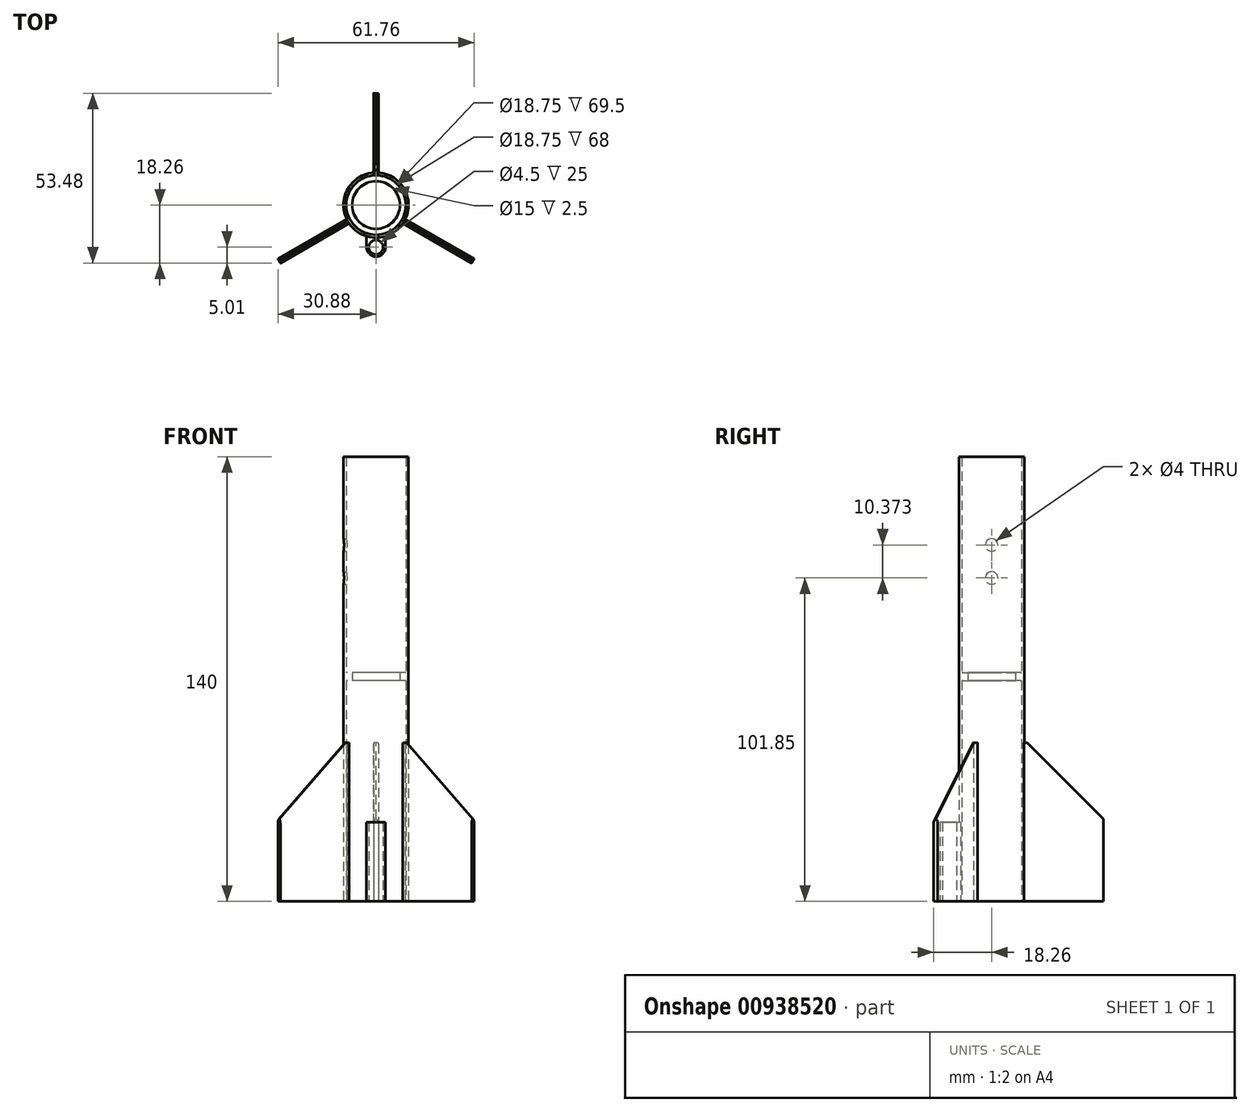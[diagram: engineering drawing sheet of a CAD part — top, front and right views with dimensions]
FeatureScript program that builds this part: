
annotation { "Feature Type Name" : "Feature", "Feature Type Description" : "" }
export const myFeature = defineFeature(function(context is Context, id is Id, definition is map)
    precondition{}
    {
        {
            var Q0;
            Q0=qCreatedBy(makeId("Top.planeOp"),FACE);
            var sketch = newSketch(context, id + "F0", { "sketchPlane" : qUnion([Q0])});
            skCircle(sketch, "E0", {"center": v(0, 0) * mm, "radius": 9.38 * mm});
            skCircle(sketch, "E1", {"center": v(0, 0) * mm, "radius": 10.25 * mm});
            skCircle(sketch, "E2", {"center": v(0, -13.25) * mm, "radius": 2.25 * mm});
            skCircle(sketch, "E3", {"center": v(0, -13.25) * mm, "radius": 3 * mm});
            skLineSegment(sketch, "E4", {"start": v(-3, -13.25) * mm, "end": v(-3, -9.8) * mm});
            skLineSegment(sketch, "E5", {"start": v(3, -13.25) * mm, "end": v(3, -9.8) * mm});
            skLineSegment(sketch, "E6.bottom", {"start": v(-0.75, 10.22) * mm, "end": v(0.75, 10.22) * mm, "construction": true});
            skLineSegment(sketch, "E6.top", {"start": v(-0.75, 35.22) * mm, "end": v(0.75, 35.22) * mm});
            skLineSegment(sketch, "E6.left", {"start": v(-0.75, 10.22) * mm, "end": v(-0.75, 35.22) * mm});
            skLineSegment(sketch, "E6.right", {"start": v(0.75, 10.22) * mm, "end": v(0.75, 35.22) * mm});
            skCircle(sketch, "E7", {"center": v(0, 0) * mm, "radius": 7.5 * mm});
            skSolve(sketch);
        }
        {
            var Q0;
            Q0=makeQuery(id+"F0.imprint","IMPRINT",FACE,{"disambiguationData":[TD([[makeQuery(id+"F0.imprint","IMPRINT",EDGE,{"derivedFrom":sQuery(id+"F0.wireOp",EDGE,"E0")}),-1.0]])]});
            extrude(context, id + "F1", {"entities" : qUnion([Q0]), "depth" : 140 * mm, "offsetDistance" : 25 * mm});
        }
        {
            var Q0;
            Q0=makeQuery(id+"F0.imprint","IMPRINT",FACE,{"disambiguationData":[TD([[makeQuery(id+"F0.imprint","IMPRINT",EDGE,{"derivedFrom":sQuery(id+"F0.wireOp",EDGE,"E6.top")}),-1.0]])]});
            extrude(context, id + "F2", {"entities" : qUnion([Q0]), "operationType" : NewBodyOperationType.ADD, "depth" : 50 * mm, "offsetDistance" : 25 * mm});
        }
        {
            var Q0;
            Q0=makeQuery(id+"F2.opExtrude","CAP_EDGE",EDGE,{"disambiguationData":[OSD([sQuery(id+"F0.wireOp",EDGE,"E6.top")])],"isStart":false});
            chamfer(context, id + "F3", {"entities" : qUnion([Q0]), "width" : 24 * mm, "tangentPropagation" : true});
        }
        {
            var Q0;
            Q0=makeQuery(id+"F3.opChamfer","BLEND_EDGE",EDGE,{"blendedFrom":[makeQuery(id+"F2.opExtrude","CAP_EDGE",EDGE,{"disambiguationData":[OSD([sQuery(id+"F0.wireOp",EDGE,"E6.top")])],"isStart":false}),makeQuery(id+"F2.opExtrude","SWEPT_FACE",FACE,{"disambiguationData":[OSD([sQuery(id+"F0.wireOp",EDGE,"E6.right")])]})],"blendedInto":[makeQuery(id+"F2.opExtrude","SWEPT_FACE",FACE,{"disambiguationData":[OSD([sQuery(id+"F0.wireOp",EDGE,"E6.right")])]})]});
            var Q1;
            Q1=makeQuery(id+"F3.opChamfer","BLEND_EDGE",EDGE,{"blendedFrom":[makeQuery(id+"F2.opExtrude","CAP_EDGE",EDGE,{"disambiguationData":[OSD([sQuery(id+"F0.wireOp",EDGE,"E6.top")])],"isStart":false}),makeQuery(id+"F2.opExtrude","SWEPT_FACE",FACE,{"disambiguationData":[OSD([sQuery(id+"F0.wireOp",EDGE,"E6.left")])]})],"blendedInto":[makeQuery(id+"F2.opExtrude","SWEPT_FACE",FACE,{"disambiguationData":[OSD([sQuery(id+"F0.wireOp",EDGE,"E6.left")])]})]});
            fillet(context, id + "F4", {"entities" : qUnion([Q0, Q1]), "radius" : 1 * mm, "tangentPropagation" : true, "allowEdgeOverflow" : false});
        }
        {
            var Q0;
            Q0=makeQuery(id+"F1.opExtrude","SWEPT_BODY",BODY,{"disambiguationData":[OSD([sQuery(id+"F0.wireOp",EDGE,"E0"),sQuery(id+"F0.wireOp",EDGE,"E1")])]});
            var Q1;
            Q1=makeQuery(id+"F1.opExtrude","SWEPT_FACE",FACE,{"disambiguationData":[OSD([sQuery(id+"F0.wireOp",EDGE,"E0")])]});
            circularPattern(context, id + "F5", {"entities" : qUnion([Q0]), "axis" : qUnion([Q1]), "angle" : 360 * degree, "instanceCount" : 3, "equalSpace" : true});
        }
        {
            var Q0;
            Q0=makeQuery(id+"F0.imprint","IMPRINT",FACE,{"disambiguationData":[TD([[makeQuery(id+"F0.imprint","IMPRINT",EDGE,{"derivedFrom":sQuery(id+"F0.wireOp",EDGE,"E2")}),-1.0]])]});
            var Q1;
            {var subQ0=sQuery(id+"F0.wireOp",EDGE,"E4");Q1=makeQuery(id+"F0.imprint","IMPRINT",FACE,{"disambiguationData":[TD([[makeQuery(id+"F0.imprint","IMPRINT",EDGE,{"derivedFrom":subQ0}),-1.0]])]});}
            var Q2;
            {var subQ0=sQuery(id+"F0.wireOp",EDGE,"E5");Q2=makeQuery(id+"F0.imprint","IMPRINT",FACE,{"disambiguationData":[TD([[makeQuery(id+"F0.imprint","IMPRINT",EDGE,{"derivedFrom":subQ0}),1.0]])]});}
            extrude(context, id + "F6", {"entities" : qUnion([Q0, Q1, Q2]), "operationType" : NewBodyOperationType.ADD, "depth" : 10 * mm, "offsetDistance" : 25 * mm});
        }
        {
            var Q0;
            Q0=makeQuery(id+"F0.imprint","IMPRINT",FACE,{"disambiguationData":[TD([[makeQuery(id+"F0.imprint","IMPRINT",EDGE,{"derivedFrom":sQuery(id+"F0.wireOp",EDGE,"E0")}),1.0]])]});
            extrude(context, id + "F7", {"entities" : qUnion([Q0]), "operationType" : NewBodyOperationType.ADD, "depth" : 72 * mm, "offsetDistance" : 25 * mm, "hasSecondDirection" : true, "secondDirectionOppositeDirection" : false, "secondDirectionDepth" : 69.5 * mm});
        }
        {
            var Q0;
            Q0=makeQuery(id+"F0.imprint","IMPRINT",FACE,{"disambiguationData":[TD([[makeQuery(id+"F0.imprint","IMPRINT",EDGE,{"derivedFrom":sQuery(id+"F0.wireOp",EDGE,"E2")}),-1.0]])]});
            var Q1;
            {var subQ0=sQuery(id+"F0.wireOp",EDGE,"E5");Q1=makeQuery(id+"F0.imprint","IMPRINT",FACE,{"disambiguationData":[TD([[makeQuery(id+"F0.imprint","IMPRINT",EDGE,{"derivedFrom":subQ0}),1.0]])]});}
            var Q2;
            {var subQ0=sQuery(id+"F0.wireOp",EDGE,"E4");Q2=makeQuery(id+"F0.imprint","IMPRINT",FACE,{"disambiguationData":[TD([[makeQuery(id+"F0.imprint","IMPRINT",EDGE,{"derivedFrom":subQ0}),-1.0]])]});}
            extrude(context, id + "F8", {"entities" : qUnion([Q0, Q1, Q2]), "operationType" : NewBodyOperationType.ADD, "depth" : 25 * mm, "offsetDistance" : 25 * mm});
        }
        {
            var Q0;
            Q0=qCreatedBy(makeId("Right.planeOp"),FACE);
            var sketch = newSketch(context, id + "F9", { "sketchPlane" : qUnion([Q0])});
            skCircle(sketch, "E8", {"center": v(0, 112.22) * mm, "radius": 2 * mm});
            skCircle(sketch, "E9", {"center": v(0, 101.85) * mm, "radius": 2 * mm});
            skSolve(sketch);
        }
        {
            var Q0;
            Q0=makeQuery(id+"F9.imprint","IMPRINT",FACE,{"disambiguationData":[TD([[makeQuery(id+"F9.imprint","IMPRINT",EDGE,{"derivedFrom":sQuery(id+"F9.wireOp",EDGE,"E8")}),1.0]])]});
            var Q1;
            Q1=makeQuery(id+"F9.imprint","IMPRINT",FACE,{"disambiguationData":[TD([[makeQuery(id+"F9.imprint","IMPRINT",EDGE,{"derivedFrom":sQuery(id+"F9.wireOp",EDGE,"E9")}),1.0]])]});
            extrude(context, id + "F10", {"entities" : qUnion([Q0, Q1]), "operationType" : NewBodyOperationType.REMOVE, "oppositeDirection" : true, "depth" : 25 * mm, "offsetDistance" : 25 * mm});
        }
    });
